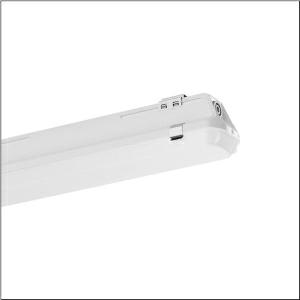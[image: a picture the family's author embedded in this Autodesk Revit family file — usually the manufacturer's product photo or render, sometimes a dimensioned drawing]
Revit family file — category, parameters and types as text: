
# Revit family: monsun_r__11_emergency_51fp107p437h3g_44d6
name_source: partatom
category: Lighting Fixtures
units: mm (PartAtom-declared; Revit-internal decimal feet)

## family parameters
Cut with Voids When Loaded = No
Host = Face
Light Source = No
Part Type = Normal
Room Calculation Point = No
Round Connector Dimension = Use Diameter
Shared = No

## types (1)
- Monsun® 11 emergency (1 x LED, 3840 lm, 24.5 W, 4000K)
    Apparent Load = 25 VA
    CIE Flux Codes = 47 77 93 94 100
    Color Rendering = 80
    Color Temperature = 4000K
    Default Elevation = 1800 mm
    Description = Monsun® 11 emergency, damp-proof luminaire, chain hanger, primary optical cover: enclosure, of PMMA, light emission: direct distribution, primary light characteristic: symmetric, installation type: suspended mounting, surface-mounted, horizontal mounting, vertical mounting, LED, rated luminous flux: 3.840lm, luminous efficacy: 157lm/W, light colour: 840, colour temperature: 4000K, control gear: ECG, with terminal, 4-pole, max. 2.5mm², mains connection: 220..240V, AC, 50/60Hz, rated input power: 25W, control gear: single battery element, battery: NiCd, 4,5Ah, mains connection: 230V, 50Hz, luminaire housing, of glass-fibre reinforced polyester, uncoated, bright grey, incl. chain hanger, length: 1.590mm, width: 90mm, height: 88mm, clip for enclosure, of stainless steel (V2A), ceiling mounting element, of stainless steel (V2A), chain hanger, of stainless steel (V2A), protection rating (complete): IP66, insulation class (complete): insulation class I (protective earthing), certification: CE, UKCA, protection symbol: D, impact resistance: IK04, permissible operating ambient temperature: +5..+35°C, standard: EN 50419, EN 60598-2-1, EN 60598-2-22, no direct snow, no direct sun, no direct rain, for indoor or canopied outdoor use, corresponds to IFS (International Featured Standards) requirements for safety and quality in the food industry, contact your sales advisor before using the luminaires in applications with unclear chemical exposure, large temperature fluctuations or condensation-forming humidity, LABS conformity tested according to VDMA 24364:2018-05, packaging unit: 1 piece
    Height = 89 mm
    Lamp = 1 x LED
    Lamp Light Flux = 3840 lm
    Lamp Power = 24.5 W
    Lamp count = 1
    Length = 1590 mm
    Luminous efficacy = 157 lm/W
    Manufacturer = Siteco
    ModVariant = No
    Model = 51FP107P437H3G
    Mounting Place = Ceiling
    Mounting Type = Surface mounted
    Number of Poles = 1
    OnlyDefault = Yes
    Power Factor = 1
    Product Name = Monsun® 11 emergency
    Product group = damp-proof luminaire
    ProductGroupID = 300
    Protection Class = Protection class I
    Protection Degree = IP 66
    RLX_Detail_Level = 1
    RLX_Emergency_Light_Flux = 0 lm
    RLX_Emergency_Type = 0
    RLX_Emergency_Type_DB = No
    RlxData = <blob elided: 89333 chars, md5=f30e24cf>
    Socket = socket
    Standby Power = 0 W
    System Light Flux = 3840 lm
    System Power = 25 W
    Type Comments = Product without accessories
    Type Image = l_1004748.jpg
    URL = http://relux.com
    VarID = ---
    Voltage = 0 V
    Weight = 0.00 kg
    Width = 90 mm

## geometry (parser evidence)
native form markers: Blend x4, Sweep x12
no freeform markers — native parametric forms only
